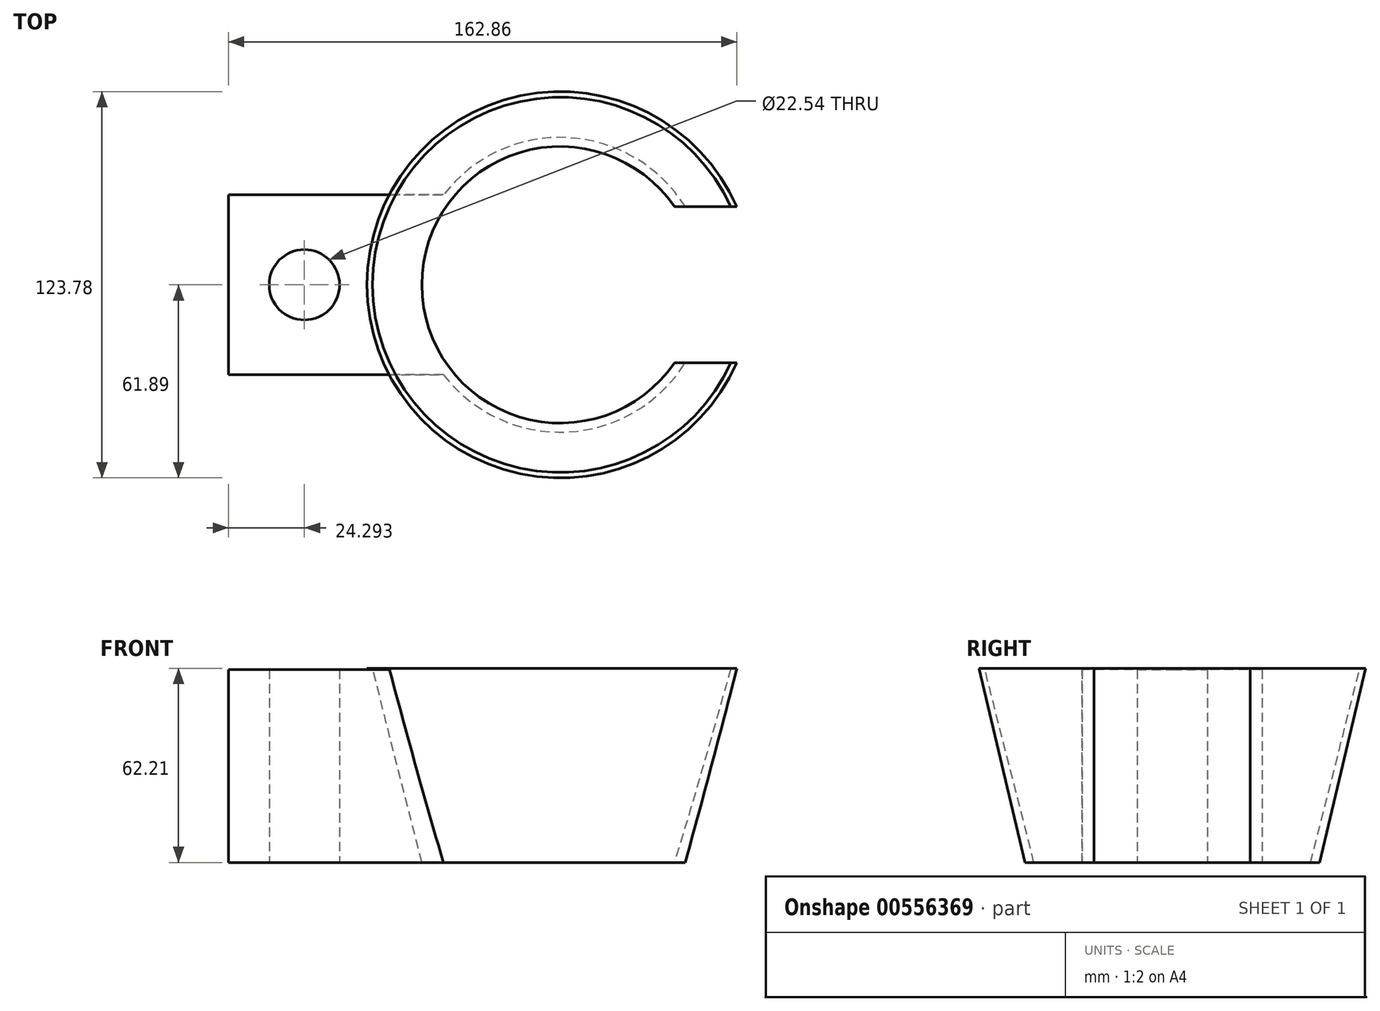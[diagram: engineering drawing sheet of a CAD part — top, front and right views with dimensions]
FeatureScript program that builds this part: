
annotation { "Feature Type Name" : "Feature", "Feature Type Description" : "" }
export const myFeature = defineFeature(function(context is Context, id is Id, definition is map)
    precondition{}
    {
        {
            var Q0;
            Q0=qCreatedBy(makeId("Front.planeOp"),FACE);
            var sketch = newSketch(context, id + "F0", { "sketchPlane" : qUnion([Q0])});
            skLineSegment(sketch, "E0", {"start": v(61.9, 62.2) * mm, "end": v(47.2, 0) * mm});
            skLineSegment(sketch, "E1", {"start": v(61.9, 62.2) * mm, "end": v(0, 62.5) * mm});
            skLineSegment(sketch, "E2", {"start": v(0, 0) * mm, "end": v(47.2, 0) * mm});
            skLineSegment(sketch, "E3", {"start": v(0, 0) * mm, "end": v(0, 62.5) * mm});
            skSolve(sketch);
        }
        {
            var Q0;
            Q0=makeQuery(id+"F0.imprint","IMPRINT",FACE,{"disambiguationData":[TD([[makeQuery(id+"F0.imprint","IMPRINT",EDGE,{"derivedFrom":sQuery(id+"F0.wireOp",EDGE,"E0")}),-1.0]])]});
            var Q1;
            Q1=sQuery(id+"F0.wireOp",EDGE,"E3");
            revolve(context, id + "F1", {"surfaceOperationType" : NewSurfaceOperationType.NEW, "entities" : qUnion([Q0]), "axis" : qUnion([Q1]), "revolveType" : RevolveType.FULL});
        }
        {
            var Q0;
            Q0=qCreatedBy(makeId("Right.planeOp"),FACE);
            cPlane(context, id + "F2", {"entities" : qUnion([Q0]), "cplaneType" : CPlaneType.OFFSET, "offset" : 29 * mm, "width" : 150 * mm, "height" : 150 * mm});
        }
        {
            var Q0;
            Q0=qCreatedBy(id+"F2.planeOp",FACE);
            var sketch = newSketch(context, id + "F3", { "sketchPlane" : qUnion([Q0])});
            skLineSegment(sketch, "E4.bottom", {"start": v(-25, 66.98) * mm, "end": v(25, 66.98) * mm});
            skLineSegment(sketch, "E4.top", {"start": v(-25, -9.07) * mm, "end": v(25, -9.07) * mm});
            skLineSegment(sketch, "E4.left", {"start": v(-25, 66.98) * mm, "end": v(-25, -9.07) * mm});
            skLineSegment(sketch, "E4.right", {"start": v(25, 66.98) * mm, "end": v(25, -9.07) * mm});
            skLineSegment(sketch, "E5", {"start": v(0, 0) * mm, "end": v(0, 70.47) * mm, "construction": true});
            skSolve(sketch);
        }
        {
            var Q0;
            Q0 = qSketchRegion(id + "F3", true);
            extrude(context, id + "F4", {"entities" : qUnion([Q0]), "operationType" : NewBodyOperationType.REMOVE, "depth" : 61.9 * mm, "offsetDistance" : 25 * mm});
        }
        {
            var Q0;
            Q0=qCreatedBy(makeId("Top.planeOp"),FACE);
            var sketch = newSketch(context, id + "F5", { "sketchPlane" : qUnion([Q0])});
            skLineSegment(sketch, "E6", {"start": v(-106.24, 28.82) * mm, "end": v(-106.24, -28.82) * mm});
            skLineSegment(sketch, "E7", {"start": v(-106.24, -28.82) * mm, "end": v(-28.7, -28.82) * mm});
            skLineSegment(sketch, "E8", {"start": v(-106.24, 0) * mm, "end": v(0, 0) * mm, "construction": true});
            skCircle(sketch, "E9", {"center": v(-81.95, 0) * mm, "radius": 11.27 * mm});
            skLineSegment(sketch, "E10", {"start": v(-27.74, 28.82) * mm, "end": v(-106.24, 28.82) * mm});
            skArc(sketch, "E11", {"start": v(-27.74, 28.82) * mm, "mid": v(-40.03, 0.2) * mm, "end": v(-28.7, -28.82) * mm});
            skSolve(sketch);
        }
        {
            var Q0;
            Q0=makeQuery(id+"F5.imprint","IMPRINT",FACE,{"disambiguationData":[TD([[makeQuery(id+"F5.imprint","IMPRINT",EDGE,{"derivedFrom":sQuery(id+"F5.wireOp",EDGE,"E6")}),1.0]])]});
            extrude(context, id + "F6", {"entities" : qUnion([Q0]), "operationType" : NewBodyOperationType.ADD, "depth" : 61.8 * mm, "offsetDistance" : 25 * mm});
        }
        {
            var Q0;
            Q0=qCreatedBy(makeId("Front.planeOp"),FACE);
            var sketch = newSketch(context, id + "F7", { "sketchPlane" : qUnion([Q0])});
            skLineSegment(sketch, "E12", {"start": v(0, 0) * mm, "end": v(0, 62.71) * mm});
            skLineSegment(sketch, "E13", {"start": v(0, 62.71) * mm, "end": v(60.24, 62.71) * mm});
            skLineSegment(sketch, "E14", {"start": v(60.24, 62.71) * mm, "end": v(44.32, 0) * mm});
            skLineSegment(sketch, "E15", {"start": v(44.32, 0) * mm, "end": v(0, 0) * mm});
            skSolve(sketch);
        }
        {
            var Q0;
            Q0 = qSketchRegion(id + "F7", true);
            var Q1;
            Q1=sQuery(id+"F7.wireOp",EDGE,"E12");
            revolve(context, id + "F8", {"operationType" : NewBodyOperationType.REMOVE, "surfaceOperationType" : NewSurfaceOperationType.NEW, "entities" : qUnion([Q0]), "axis" : qUnion([Q1]), "revolveType" : RevolveType.FULL, "oppositeDirection" : true});
        }
    });
